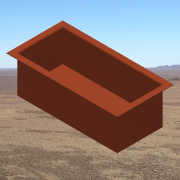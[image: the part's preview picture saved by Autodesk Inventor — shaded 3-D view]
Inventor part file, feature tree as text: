
AUTODESK INVENTOR PART (.ipt)
format: ipt  version: 2014 SP1 (Build 180222100, 222)  size: 137,216 bytes
history: native  units: in
note: dims shown in document units (in); Inventor stores cm internally (conversion verified against a paired STEP export)
features: extrude x3, sketch x3
ambient origin geometry x8: Origin, YZ Plane, XZ Plane, XY Plane, X Axis, Y Axis, Z Axis, Center Point
bodies: Solid1 (feature_tree)
feature tree (6):
  extrude  "Extrusion1"  Depth=10.0in
  extrude  "Extrusion2"  Depth=1.1811in
  extrude  "Extrusion4"  Depth=0.1in
  sketch  "Sketch1"  dims[d0=22.0in d1=10.0in]
  sketch  "Sketch2"  dims[d2=8.0in d3=0.0in d4=1.1811in]
  sketch  "Sketch4"  dims[d5=0.1in d6=0.0in d9=0.1in d10=6.9in d11=0.0in]
